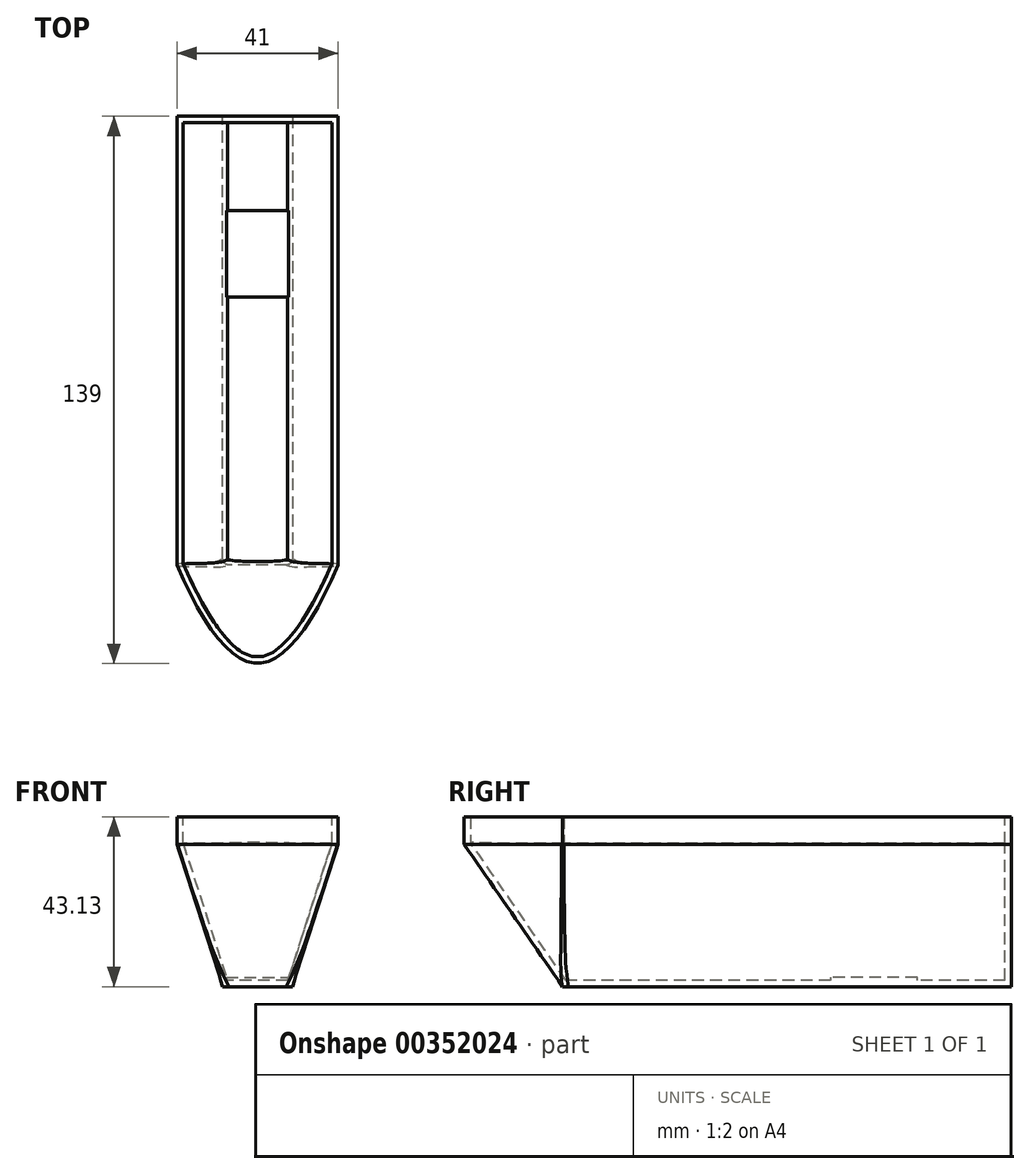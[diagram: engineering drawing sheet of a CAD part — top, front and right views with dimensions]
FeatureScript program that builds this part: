
annotation { "Feature Type Name" : "Feature", "Feature Type Description" : "" }
export const myFeature = defineFeature(function(context is Context, id is Id, definition is map)
    precondition{}
    {
        {
            var Q0;
            Q0=qCreatedBy(makeId("Top.planeOp"),FACE);
            cPlane(context, id + "F0", {"entities" : qUnion([Q0]), "cplaneType" : CPlaneType.OFFSET, "offset" : 36.12 * mm, "width" : 150 * mm, "height" : 150 * mm});
        }
        {
            var Q0;
            Q0=qCreatedBy(id+"F0.planeOp",FACE);
            var sketch = newSketch(context, id + "F1", { "sketchPlane" : qUnion([Q0])});
            skLineSegment(sketch, "E0", {"start": v(20.5, 114) * mm, "end": v(-20.5, 114) * mm});
            skLineSegment(sketch, "E1", {"start": v(20.5, 114) * mm, "end": v(20.5, 0) * mm});
            skLineSegment(sketch, "E2", {"start": v(-20.5, 114) * mm, "end": v(-20.5, 0) * mm});
            skPoint(sketch, "E3", {"position": v(0, -25) * mm});
            skFitSpline(sketch, "E4", {"points": [v(20.5, 0) * mm, v(0, -25) * mm, v(-20.5, 0) * mm], "startDerivative": vector(-39, -90) * mm, "endDerivative": vector(-39, 90) * mm});
            skSolve(sketch);
        }
        {
            var Q0;
            Q0=qCreatedBy(makeId("Top.planeOp"),FACE);
            var sketch = newSketch(context, id + "F2", { "sketchPlane" : qUnion([Q0])});
            skPoint(sketch, "E5", {"position": v(0, 0) * mm});
            skLineSegment(sketch, "E6", {"start": v(-8.83, 114) * mm, "end": v(8.83, 114) * mm});
            skLineSegment(sketch, "E7", {"start": v(8.83, 114) * mm, "end": v(8.83, 0) * mm});
            skLineSegment(sketch, "E8", {"start": v(8.83, 0) * mm, "end": v(-8.83, 0) * mm});
            skLineSegment(sketch, "E9", {"start": v(-8.83, 0) * mm, "end": v(-8.83, 114) * mm});
            skSolve(sketch);
        }
        {
            var Q0;
            Q0=makeQuery(id+"F1.imprint","IMPRINT",FACE,{"disambiguationData":[TD([[makeQuery(id+"F1.imprint","IMPRINT",EDGE,{"derivedFrom":sQuery(id+"F1.wireOp",EDGE,"E0")}),1.0]])]});
            var Q1;
            Q1=makeQuery(id+"F2.imprint","IMPRINT",FACE,{"disambiguationData":[TD([[makeQuery(id+"F2.imprint","IMPRINT",EDGE,{"derivedFrom":sQuery(id+"F2.wireOp",EDGE,"E6")}),-1.0]])]});
            loft(context, id + "F3", {"sheetProfilesArray" : [{ "sheetProfileEntities" : qUnion([Q0]) }, { "sheetProfileEntities" : qUnion([Q1]) }]});
        }
        {
            var Q0;
            Q0=makeQuery(id+"F1.imprint","IMPRINT",FACE,{"disambiguationData":[TD([[makeQuery(id+"F1.imprint","IMPRINT",EDGE,{"derivedFrom":sQuery(id+"F1.wireOp",EDGE,"E0")}),1.0]])]});
            extrude(context, id + "F4", {"entities" : qUnion([Q0]), "operationType" : NewBodyOperationType.ADD, "depth" : 7 * mm});
        }
        {
            var Q0;
            Q0=makeQuery(id+"F4.opExtrude","CAP_FACE",FACE,{"disambiguationData":[OSD([sQuery(id+"F1.wireOp",EDGE,"E0"),sQuery(id+"F1.wireOp",EDGE,"E1"),sQuery(id+"F1.wireOp",EDGE,"E2"),sQuery(id+"F1.wireOp",EDGE,"E4")])],"isStart":false});
            shell(context, id + "F5", {"entities" : qUnion([Q0]), "thickness" : 1.6 * mm});
        }
        {
            var Q0;
            Q0=makeQuery(id+"F3.opLoft","SWEPT_EDGE",EDGE,{"disambiguationData":[OSD([sQuery(id+"F1.wireOp",EDGE,"E1"),sQuery(id+"F1.wireOp",EDGE,"E4"),sQuery(id+"F2.wireOp",EDGE,"E7"),sQuery(id+"F2.wireOp",EDGE,"E8")])]});
            var Q1;
            Q1=makeQuery(id+"F3.opLoft","SWEPT_EDGE",EDGE,{"disambiguationData":[OSD([sQuery(id+"F1.wireOp",EDGE,"E2"),sQuery(id+"F1.wireOp",EDGE,"E4"),sQuery(id+"F2.wireOp",EDGE,"E8"),sQuery(id+"F2.wireOp",EDGE,"E9")])]});
            fillet(context, id + "F6", {"entities" : qUnion([Q0, Q1]), "radius" : 1.6 * mm, "tangentPropagation" : true, "allowEdgeOverflow" : false});
        }
        {
            var Q0;
            Q0=qCreatedBy(makeId("Top.planeOp"),FACE);
            var sketch = newSketch(context, id + "F7", { "sketchPlane" : qUnion([Q0])});
            skLineSegment(sketch, "E10", {"start": v(-8.83, 90.1) * mm, "end": v(8.83, 90.1) * mm});
            skLineSegment(sketch, "E11", {"start": v(8.83, 90.1) * mm, "end": v(8.83, 68.1) * mm});
            skLineSegment(sketch, "E12", {"start": v(8.83, 68.1) * mm, "end": v(-8.83, 68.1) * mm});
            skLineSegment(sketch, "E13", {"start": v(-8.83, 68.1) * mm, "end": v(-8.83, 90.1) * mm});
            skSolve(sketch);
        }
        {
            var Q0;
            Q0=makeQuery(id+"F7.imprint","IMPRINT",FACE,{"disambiguationData":[TD([[makeQuery(id+"F7.imprint","IMPRINT",EDGE,{"derivedFrom":sQuery(id+"F7.wireOp",EDGE,"E10")}),-1.0]])]});
            extrude(context, id + "F8", {"entities" : qUnion([Q0]), "operationType" : NewBodyOperationType.ADD, "depth" : 2.4 * mm});
        }
    });
